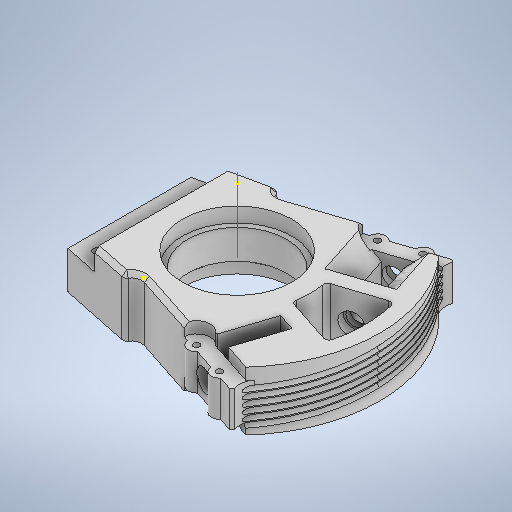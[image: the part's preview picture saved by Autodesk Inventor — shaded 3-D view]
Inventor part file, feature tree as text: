
AUTODESK INVENTOR PART (.ipt)
format: ipt  version: 2025.2 (Build 292293000, 293)  size: 1,875,456 bytes
history: native  units: mm
features: sketch x39, extrude x33, helix x12, projected_geometry x4, chamfer x3, fillet x2, other x2, plane x1, mirror x1
ambient origin geometry x8: Origin, YZ Plane, XZ Plane, XY Plane, X Axis, Y Axis, Z Axis, Center Point
bodies: Solid1 (feature_tree)
feature tree (97):
  extrude  "Extrusion1"  Depth=28.0mm TaperAngle=0.0deg
  sketch  "Sketch2"  dims[d7=8.5mm d9=60.0deg]
  extrude  "Extrusion2"  Depth=70.0mm
  extrude  "Extrusion3"  TaperAngle=60.0deg  [1 undecoded]
  extrude  "Extrusion4"  TaperAngle=0.0deg  [1 undecoded]
  extrude  "Extrusion5"  Depth=10.0mm
  extrude  "Extrusion6"  TaperAngle=0.0deg  [1 undecoded]
  extrude  "Extrusion7"  Depth=7.0mm TaperAngle=0.0deg
  extrude  "Extrusion8"  Depth=7.0mm TaperAngle=0.0deg
  extrude  "Extrusion9"  Depth=7.0mm
  fillet  "Fillet1"  Radius=7.0mm
  extrude  "Extrusion10"  TaperAngle=0.0deg  [1 undecoded]
  extrude  "Extrusion11"  Depth=7.0mm
  extrude  "Extrusion12"  Depth=7.0mm
  extrude  "Extrusion13"  Depth=2.0mm
  chamfer  "Chamfer3"  Distance=5.5mm
  extrude  "Extrusion14"  Depth=5.5mm TaperAngle=0.0deg
  extrude  "Extrusion15"  Depth=5.5mm TaperAngle=0.0deg
  extrude  "Extrusion16"  Depth=2.0mm
  extrude  "Extrusion17"  Depth=4.0mm TaperAngle=0.0deg
  extrude  "Extrusion18"  TaperAngle=0.0deg  [1 undecoded]
  extrude  "Extrusion19"  Depth=4.0mm TaperAngle=0.0deg
  chamfer  "Chamfer4"  Distance=10.0mm
  extrude  "Extrusion20"  Depth=5.5mm TaperAngle=0.0deg
  extrude  "Extrusion21"  Depth=10.0mm TaperAngle=0.0deg
  sketch  "Sketch23"  dims[d76=5.1mm]
  extrude  "Extrusion22"  Depth=3.0mm
  extrude  "Extrusion23"  Depth=3.0mm
  extrude  "Extrusion24"  TaperAngle=0.0deg  [1 undecoded]
  extrude  "Extrusion25"  Depth=4.0mm
  plane  "Work Plane1"
  sketch  "Sketch29"  dims[d89=3.0mm d90=3.0mm]
  helix  "Coil2"  [1 undecoded]
  helix  "Coil3"  [1 undecoded]
  sketch  "Sketch30"  dims[d91=3.0mm d92=3.0mm]
  helix  "Coil4"  [1 undecoded]
  helix  "Coil5"  [1 undecoded]
  helix  "Coil6"  [1 undecoded]
  helix  "Coil7"  [1 undecoded]
  helix  "Coil8"  [1 undecoded]
  helix  "Coil9"  [1 undecoded]
  helix  "Coil10"  [1 undecoded]
  helix  "Coil11"  [1 undecoded]
  helix  "Coil12"  [1 undecoded]
  helix  "Coil13"  [1 undecoded]
  extrude  "Extrusion26"  Depth=5.0mm
  extrude  "Extrusion27"  Depth=10.0mm
  sketch  "Sketch35"  dims[d133=24.0mm d134=30.75mm d135=5.0mm d136=0.0mm d137=90.0deg d138=90.0deg d139=0.0mm d140=0.0mm d141=5.625mm d142=2.5mm]
  extrude  "Extrusion28"  Depth=10.0mm TaperAngle=0.0deg
  extrude  "Extrusion29"  Depth=0.75mm TaperAngle=0.0deg
  extrude  "Extrusion30"  Depth=0.5mm
  sketch  "Sketch41"  dims[d168=24.0mm d169=27.25mm d170=5.0mm d171=0.0mm d172=90.0deg d173=90.0deg d174=0.0mm d175=0.0mm]
  extrude  "Extrusion31"  Depth=18.0mm TaperAngle=0.0deg
  extrude  "Extrusion32"  Depth=18.0mm TaperAngle=0.0deg
  fillet  "Fillet2"  Radius=4.0mm
  extrude  "Extrusion33"  Depth=4.0mm
  chamfer  "Chamfer6"  Distance=12.0mm
  mirror  "Mirror1"
  sketch  "Sketch1"  dims[d0=136.0mm d1=28.0mm d2=0.0mm]
  sketch  "Sketch3"  dims[d10=1.22173mm d11=0.0mm d12=0.0mm]
  sketch  "Sketch4"  dims[d13=10.0mm d14=0.0mm d15=50.0mm]
  sketch  "Sketch6"  dims[d17=1.5mm d18=0.0mm d19=0.0mm]
  sketch  "Sketch7"  dims[d20=52.1mm d21=7.0mm d22=0.0mm]
  sketch  "Sketch8"  dims[d23=7.0mm d24=0.0mm d25=14.2mm d26=0.0mm]
  sketch  "Sketch9"  dims[d27=8.5mm d28=14.75mm d30=7.0mm]
  sketch  "Sketch10"  dims[d31=24.0mm d32=0.0mm d33=0.0mm]
  sketch  "Sketch11"  dims[d36=7.0mm d37=7.0mm]
  sketch  "Sketch12"  dims[d38=7.0mm d39=9.0mm]
  sketch  "Sketch13"  dims[d40=0.0mm d41=0.0mm d42=2.0mm]
  sketch  "Sketch15"  dims[d43=8.0mm d44=5.5mm d45=0.0mm]
  sketch  "Sketch16"  dims[d49=8.0mm d50=5.5mm d51=0.0mm]
  sketch  "Sketch17"  dims[d55=5.5mm d56=0.0mm d57=5.5mm d58=0.0mm]
  sketch  "Sketch18"  dims[d61=3.75mm d62=2.0mm d63=45.0deg d64=8.0mm]
  sketch  "Sketch19"  dims[d65=10.2mm d66=4.0mm d67=0.0mm]
  sketch  "Sketch20"  dims[d68=1.0mm d69=0.0mm d70=0.0mm]
  sketch  "Sketch21"  dims[d71=4.0mm d72=0.0mm d73=4.0mm d74=0.0mm]
  sketch  "Sketch22"  dims[d75=3.0mm]
  sketch  "Sketch24"  dims[d77=2.0mm]
  sketch  "Sketch25"  dims[d78=2.5mm d79=10.0mm d80=0.0mm]
  sketch  "Sketch26"  dims[d81=2.5mm d82=5.5mm d83=0.0mm]
  sketch  "Sketch27"  dims[d84=5.5mm d85=2.0mm d86=45.0deg d87=10.0mm d88=0.0mm]
  other  "Work Axis1"
  sketch  "Sketch31"  dims[d93=0.0mm d94=0.0mm d95=0.0mm d96=0.0mm]
  projected_geometry  "Projected Loop1"
  sketch  "Sketch Rectangular Pattern1"  dims[d3=6.981317mm d5=70.0mm]
  sketch  "Sketch32"  dims[d97=10.2mm d98=4.25mm d99=4.25mm d100=8.5mm d101=8.5mm d102=5.0mm d103=4.0mm d104=0.0mm d105=0.0mm d106=1.0mm d107=5.0mm d108=0.0mm d109=4.0mm d110=0.0mm d111=-7.679449mm d123=4.875mm d124=2.5mm]
  projected_geometry  "Projected Loop2"
  projected_geometry  "Projected Loop3"
  sketch  "Sketch34"  dims[d125=24.0mm d126=30.75mm d127=10.0mm d128=0.0mm d129=90.0deg d130=90.0deg d131=0.0mm d132=0.0mm]
  sketch  "Sketch36"  dims[d143=24.0mm d144=30.75mm d145=5.0mm d146=0.0mm d147=90.0deg d148=90.0deg d149=0.0mm d150=0.0mm]
  sketch  "Sketch37"  dims[d151=24.0mm d152=30.75mm d153=5.0mm d154=0.0mm d155=90.0deg d156=90.0deg d157=0.0mm d158=0.0mm d159=4.875mm]
  sketch  "Sketch38"  dims[d160=2.5mm d161=50.0mm d163=3.0mm d164=10.0mm d166=10.0mm]
  projected_geometry  "Projected Loop5"
  sketch  "Sketch42"  dims[d176=24.0mm d177=27.25mm d178=5.0mm d179=0.0mm d180=90.0deg d181=90.0deg d182=0.0mm d183=0.0mm]
  sketch  "Sketch43"  dims[d184=24.0mm d185=27.25mm d186=5.0mm d187=0.0mm d188=90.0deg d189=90.0deg d190=0.0mm d191=0.0mm]
  sketch  "Sketch44"  dims[d192=24.0mm d193=27.25mm d194=5.0mm d195=0.0mm d196=90.0deg d197=90.0deg d198=0.0mm d199=0.0mm d200=24.0mm d201=27.25mm d202=5.0mm d203=0.0mm d204=90.0deg d205=90.0deg d206=0.0mm d207=0.0mm d208=24.0mm d209=27.25mm d210=5.0mm d211=0.0mm d212=90.0deg d213=90.0deg d214=0.0mm d215=0.0mm d216=24.0mm d217=27.25mm d218=5.0mm d219=0.0mm d220=90.0deg d221=90.0deg d222=0.0mm d223=0.0mm d224=24.0mm d225=27.25mm d226=5.0mm d227=0.0mm d228=90.0deg d229=90.0deg d230=0.0mm d231=0.0mm d232=10.0mm d233=0.0mm d234=0.75mm d235=0.0mm d236=40.0mm d237=18.0mm d238=0.0mm d239=18.0mm d240=0.0mm d241=4.0mm d242=4.0mm d244=12.0mm d245=3.0mm d246=3.0mm d247=18.5mm d248=0.0mm d250=150.0mm d251=38.0mm d253=5.0mm d254=10.0mm d255=0.0mm d256=10.0mm d257=0.0mm d258=2.0mm d259=4.0mm d260=31.027281mm d261=7.75682mm d262=0.0mm d263=0.0mm d264=17.0mm d268=2.0mm d269=2.0mm d270=45.0deg d59=0.5mm d60=0.872665mm d249=0.5mm d252=0.872665mm]
  other  "Big_drum"
note: 18 required parameter values undecoded (feature->parameter linkage not recoverable at this tier; creation-order binding heuristic only, values carry confidence <= 0.55)
